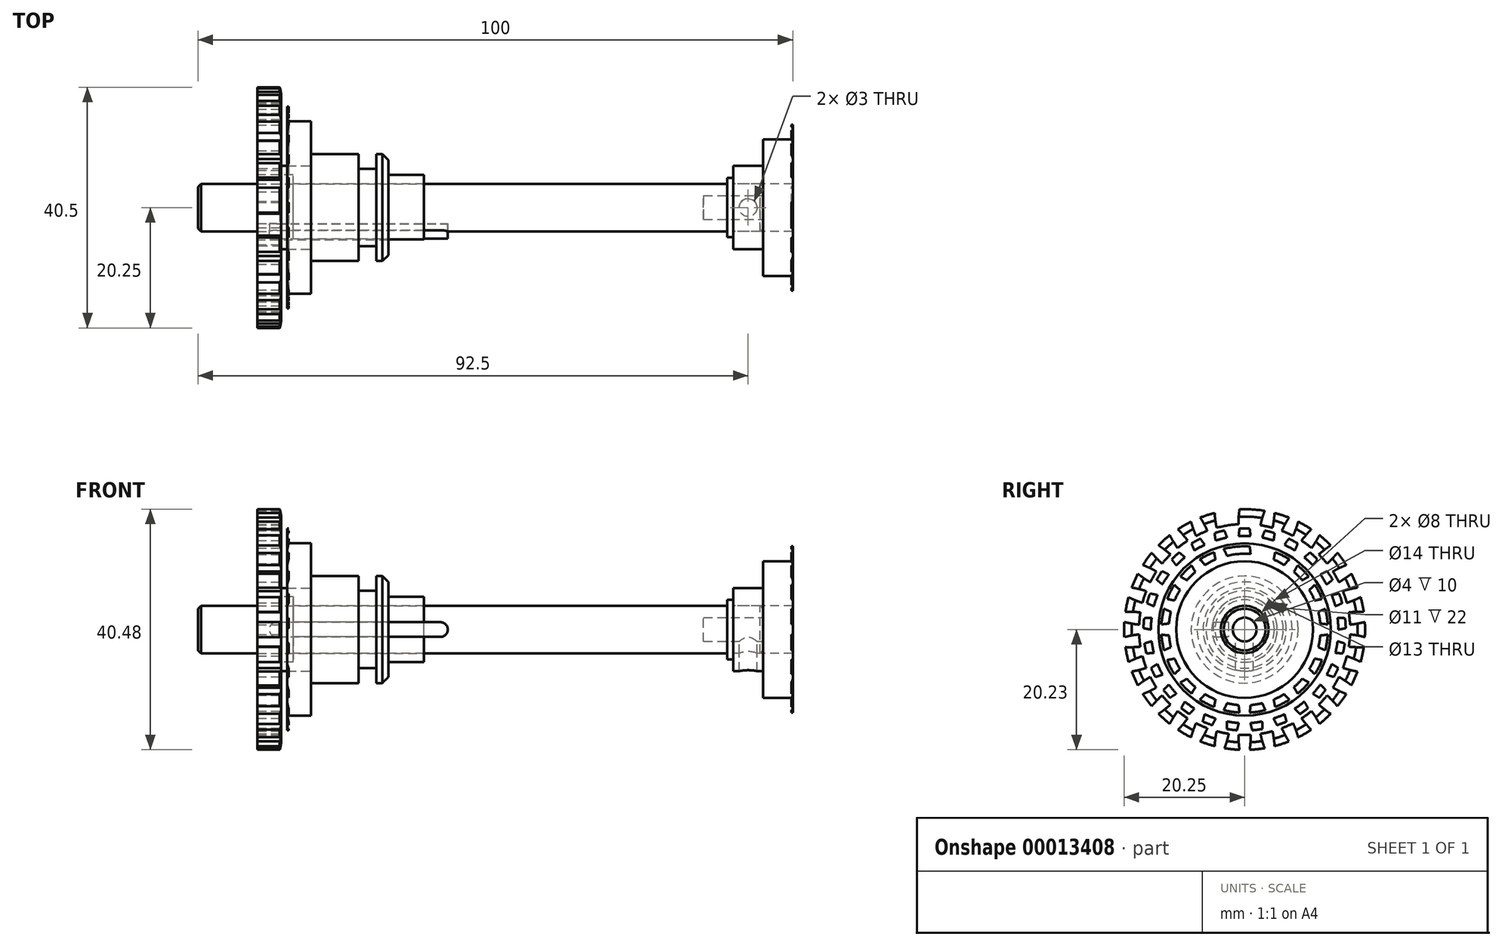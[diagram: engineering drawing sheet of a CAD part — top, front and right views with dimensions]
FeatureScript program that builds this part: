
annotation { "Feature Type Name" : "Feature", "Feature Type Description" : "" }
export const myFeature = defineFeature(function(context is Context, id is Id, definition is map)
    precondition{}
    {
        {
            var Q0;
            Q0=qCreatedBy(makeId("Right.planeOp"),FACE);
            var sketch = newSketch(context, id + "F0", { "sketchPlane" : qUnion([Q0])});
            skCircle(sketch, "E0", {"center": v(0, 0) * mm, "radius": 2 * mm});
            skCircle(sketch, "E1", {"center": v(0, 0) * mm, "radius": 4 * mm});
            skCircle(sketch, "E2", {"center": v(0, 0) * mm, "radius": 5 * mm});
            skSolve(sketch);
        }
        {
            var Q0;
            Q0=makeQuery(id+"F0.imprint","IMPRINT",FACE,{"disambiguationData":[TD([[makeQuery(id+"F0.imprint","IMPRINT",EDGE,{"derivedFrom":sQuery(id+"F0.wireOp",EDGE,"E0")}),-1.0]])]});
            var Q1;
            Q1=makeQuery(id+"F0.imprint","IMPRINT",FACE,{"disambiguationData":[TD([[makeQuery(id+"F0.imprint","IMPRINT",EDGE,{"derivedFrom":sQuery(id+"F0.wireOp",EDGE,"E0")}),1.0]])]});
            extrude(context, id + "F1", {"entities" : qUnion([Q0, Q1]), "oppositeDirection" : true, "depth" : 90 * mm});
        }
        {
            var Q0;
            Q0=makeQuery(id+"F0.imprint","IMPRINT",FACE,{"disambiguationData":[TD([[makeQuery(id+"F0.imprint","IMPRINT",EDGE,{"derivedFrom":sQuery(id+"F0.wireOp",EDGE,"E1")}),-1.0]])]});
            var Q1;
            Q1=makeQuery(id+"F0.imprint","IMPRINT",FACE,{"disambiguationData":[TD([[makeQuery(id+"F0.imprint","IMPRINT",EDGE,{"derivedFrom":sQuery(id+"F0.wireOp",EDGE,"E0")}),-1.0]])]});
            extrude(context, id + "F2", {"entities" : qUnion([Q0, Q1]), "operationType" : NewBodyOperationType.ADD, "oppositeDirection" : true, "depth" : 1 * mm});
        }
        {
            var Q0;
            Q0=makeQuery(id+"F0.imprint","IMPRINT",FACE,{"disambiguationData":[TD([[makeQuery(id+"F0.imprint","IMPRINT",EDGE,{"derivedFrom":sQuery(id+"F0.wireOp",EDGE,"E0")}),1.0]])]});
            extrude(context, id + "F3", {"entities" : qUnion([Q0]), "operationType" : NewBodyOperationType.REMOVE, "oppositeDirection" : true, "depth" : 5 * mm});
        }
        {
            var Q0;
            Q0=makeQuery(id+"F0.imprint","IMPRINT",FACE,{"disambiguationData":[TD([[makeQuery(id+"F0.imprint","IMPRINT",EDGE,{"derivedFrom":sQuery(id+"F0.wireOp",EDGE,"E0")}),-1.0]])]});
            extrude(context, id + "F4", {"entities" : qUnion([Q0]), "operationType" : NewBodyOperationType.ADD, "depth" : 5 * mm});
        }
        {
            var Q0;
            Q0=qCreatedBy(makeId("Front.planeOp"),FACE);
            cPlane(context, id + "F5", {"entities" : qUnion([Q0]), "cplaneType" : CPlaneType.OFFSET, "offset" : 4 * mm, "width" : 150 * mm, "height" : 150 * mm});
        }
        {
            var Q0;
            Q0=qCreatedBy(id+"F5.planeOp",FACE);
            var sketch = newSketch(context, id + "F6", { "sketchPlane" : qUnion([Q0])});
            skLineSegment(sketch, "E3.0", {"start": v(-90, 4) * mm, "end": v(-90, -4) * mm});
            skLineSegment(sketch, "E4", {"start": v(-90, 0) * mm, "end": v(-49.25, 0) * mm, "construction": true});
            skCircle(sketch, "E5", {"center": v(-49.25, 0) * mm, "radius": 1.25 * mm});
            skCircle(sketch, "E6", {"center": v(-76.75, 0) * mm, "radius": 1.25 * mm});
            skLineSegment(sketch, "E7", {"start": v(-76.75, 1.25) * mm, "end": v(-49.25, 1.25) * mm});
            skLineSegment(sketch, "E8", {"start": v(-76.75, -1.25) * mm, "end": v(-49.25, -1.25) * mm});
            skSolve(sketch);
        }
        {
            var Q0;
            {var subQ0=sQuery(id+"F6.wireOp",EDGE,"E6");var subQ2=makeQuery(id+"F6.imprint","INTERSECT",VERTEX,{"derivedFrom":[subQ0,sQuery(id+"F6.wireOp",EDGE,"E7")]});Q0=makeQuery(id+"F6.imprint","IMPRINT",FACE,{"disambiguationData":[TD([[makeQuery(id+"F6.imprint","IMPRINT",EDGE,{"disambiguationData":[TD([[subQ2,-1.0]])],"derivedFrom":subQ0}),1.0]])]});}
            var Q1;
            {var subQ1=sQuery(id+"F6.wireOp",EDGE,"E7");Q1=makeQuery(id+"F6.imprint","IMPRINT",FACE,{"disambiguationData":[TD([[makeQuery(id+"F6.imprint","IMPRINT",EDGE,{"derivedFrom":subQ1}),-1.0]])]});}
            var Q2;
            {var subQ0=sQuery(id+"F6.wireOp",EDGE,"E5");var subQ2=makeQuery(id+"F6.imprint","INTERSECT",VERTEX,{"derivedFrom":[subQ0,sQuery(id+"F6.wireOp",EDGE,"E7")]});Q2=makeQuery(id+"F6.imprint","IMPRINT",FACE,{"disambiguationData":[TD([[makeQuery(id+"F6.imprint","IMPRINT",EDGE,{"disambiguationData":[TD([[subQ2,-1.0]])],"derivedFrom":subQ0}),1.0]])]});}
            extrude(context, id + "F7", {"entities" : qUnion([Q0, Q1, Q2]), "operationType" : NewBodyOperationType.REMOVE, "oppositeDirection" : true, "depth" : 1.3 * mm});
        }
        {
            var Q0;
            {var subQ0=sQuery(id+"F6.wireOp",EDGE,"E6");var subQ2=makeQuery(id+"F6.imprint","INTERSECT",VERTEX,{"derivedFrom":[subQ0,sQuery(id+"F6.wireOp",EDGE,"E7")]});Q0=makeQuery(id+"F6.imprint","IMPRINT",FACE,{"disambiguationData":[TD([[makeQuery(id+"F6.imprint","IMPRINT",EDGE,{"disambiguationData":[TD([[subQ2,-1.0]])],"derivedFrom":subQ0}),1.0]])]});}
            var Q1;
            {var subQ1=sQuery(id+"F6.wireOp",EDGE,"E7");Q1=makeQuery(id+"F6.imprint","IMPRINT",FACE,{"disambiguationData":[TD([[makeQuery(id+"F6.imprint","IMPRINT",EDGE,{"derivedFrom":subQ1}),-1.0]])]});}
            var Q2;
            {var subQ0=sQuery(id+"F6.wireOp",EDGE,"E5");var subQ2=makeQuery(id+"F6.imprint","INTERSECT",VERTEX,{"derivedFrom":[subQ0,sQuery(id+"F6.wireOp",EDGE,"E7")]});Q2=makeQuery(id+"F6.imprint","IMPRINT",FACE,{"disambiguationData":[TD([[makeQuery(id+"F6.imprint","IMPRINT",EDGE,{"disambiguationData":[TD([[subQ2,-1.0]])],"derivedFrom":subQ0}),1.0]])]});}
            extrude(context, id + "F8", {"entities" : qUnion([Q0, Q1, Q2]), "endBound" : BoundingType.SYMMETRIC, "depth" : 2.5 * mm});
        }
        {
            var Q0;
            Q0=makeQuery(id+"F4.opExtrude","CAP_EDGE",EDGE,{"disambiguationData":[OSD([sQuery(id+"F0.wireOp",EDGE,"E1")])],"isStart":false});
            var Q1;
            Q1=makeQuery(id+"F1.opExtrude","CAP_EDGE",EDGE,{"disambiguationData":[OSD([sQuery(id+"F0.wireOp",EDGE,"E1")])],"isStart":false});
            chamfer(context, id + "F9", {"entities" : qUnion([Q0, Q1]), "width" : 0.5 * mm, "tangentPropagation" : true});
        }
        {
            var Q0;
            Q0=qCreatedBy(makeId("Right.planeOp"),FACE);
            cPlane(context, id + "F10", {"entities" : qUnion([Q0]), "cplaneType" : CPlaneType.OFFSET, "offset" : (48 + 15) * mm, "oppositeDirection" : true, "width" : 150 * mm, "height" : 150 * mm});
        }
        {
            var Q0;
            Q0=qCreatedBy(id+"F10.planeOp",FACE);
            var sketch = newSketch(context, id + "F11", { "sketchPlane" : qUnion([Q0])});
            skCircle(sketch, "E9.0", {"center": v(0, 0) * mm, "radius": 4 * mm});
            skLineSegment(sketch, "E9.1", {"start": v(-5.36, -1.25) * mm, "end": v(-2.75, -1.25) * mm});
            skLineSegment(sketch, "E9.2", {"start": v(-5.36, 1.25) * mm, "end": v(-2.75, 1.25) * mm});
            skCircle(sketch, "E10", {"center": v(0, 0) * mm, "radius": 5.5 * mm});
            skPoint(sketch, "E11.orphan", {"position": v(-5.25, 1.25) * mm});
            skPoint(sketch, "E12.orphan", {"position": v(-5.25, -1.25) * mm});
            skSolve(sketch);
        }
        {
            var Q0;
            {var subQ3=sQuery(id+"F11.wireOp",EDGE,"E9.1");var subQ5=sQuery(id+"F11.wireOp",EDGE,"E9.0");var subQ7=makeQuery(id+"F11.imprint","INTERSECT",VERTEX,{"derivedFrom":[subQ5,subQ3]});Q0=makeQuery(id+"F11.imprint","IMPRINT",FACE,{"disambiguationData":[TD([[makeQuery(id+"F11.imprint","IMPRINT",EDGE,{"disambiguationData":[TD([[subQ7,-1.0]])],"derivedFrom":subQ5}),-1.0]])]});}
            extrude(context, id + "F12", {"entities" : qUnion([Q0]), "endBound" : BoundingType.SYMMETRIC, "depth" : 22 * mm});
        }
        {
            var Q0;
            Q0=qCreatedBy(id+"F10.planeOp",FACE);
            var sketch = newSketch(context, id + "F13", { "sketchPlane" : qUnion([Q0])});
            skCircle(sketch, "E13.1", {"center": v(0, 0) * mm, "radius": 5.5 * mm});
            skCircle(sketch, "E14", {"center": v(0, 0) * mm, "radius": 6.5 * mm});
            skCircle(sketch, "E15", {"center": v(0, 0) * mm, "radius": 7 * mm});
            skCircle(sketch, "E16", {"center": v(0, 0) * mm, "radius": 9 * mm});
            skSolve(sketch);
        }
        {
            var Q0;
            Q0=makeQuery(id+"F13.imprint","IMPRINT",FACE,{"disambiguationData":[TD([[makeQuery(id+"F13.imprint","IMPRINT",EDGE,{"derivedFrom":sQuery(id+"F13.wireOp",EDGE,"E13.1")}),-1.0]])]});
            var Q1;
            Q1=makeQuery(id+"F13.imprint","IMPRINT",FACE,{"disambiguationData":[TD([[makeQuery(id+"F13.imprint","IMPRINT",EDGE,{"derivedFrom":sQuery(id+"F13.wireOp",EDGE,"E14")}),-1.0]])]});
            var Q2;
            Q2=makeQuery(id+"F13.imprint","IMPRINT",FACE,{"disambiguationData":[TD([[makeQuery(id+"F13.imprint","IMPRINT",EDGE,{"derivedFrom":sQuery(id+"F13.wireOp",EDGE,"E15")}),-1.0]])]});
            extrude(context, id + "F14", {"entities" : qUnion([Q0, Q1, Q2]), "depth" : 5 * mm});
        }
        {
            var Q0;
            Q0=makeQuery(id+"F13.imprint","IMPRINT",FACE,{"disambiguationData":[TD([[makeQuery(id+"F13.imprint","IMPRINT",EDGE,{"derivedFrom":sQuery(id+"F13.wireOp",EDGE,"E15")}),-1.0]])]});
            var Q1;
            Q1=makeQuery(id+"F13.imprint","IMPRINT",FACE,{"disambiguationData":[TD([[makeQuery(id+"F13.imprint","IMPRINT",EDGE,{"derivedFrom":sQuery(id+"F13.wireOp",EDGE,"E14")}),-1.0]])]});
            extrude(context, id + "F15", {"entities" : qUnion([Q0, Q1]), "operationType" : NewBodyOperationType.REMOVE, "depth" : 3 * mm});
        }
        {
            var Q0;
            Q0=makeQuery(id+"F13.imprint","IMPRINT",FACE,{"disambiguationData":[TD([[makeQuery(id+"F13.imprint","IMPRINT",EDGE,{"derivedFrom":sQuery(id+"F13.wireOp",EDGE,"E13.1")}),-1.0]])]});
            extrude(context, id + "F16", {"entities" : qUnion([Q0]), "operationType" : NewBodyOperationType.ADD, "oppositeDirection" : true, "depth" : (4 + 5 + 8) * mm});
        }
        {
            var Q0;
            Q0=makeQuery(id+"F13.imprint","IMPRINT",FACE,{"disambiguationData":[TD([[makeQuery(id+"F13.imprint","IMPRINT",EDGE,{"derivedFrom":sQuery(id+"F13.wireOp",EDGE,"E14")}),-1.0]])]});
            extrude(context, id + "F17", {"entities" : qUnion([Q0]), "operationType" : NewBodyOperationType.ADD, "oppositeDirection" : true, "depth" : (5 + 8) * mm});
        }
        {
            var Q0;
            Q0=makeQuery(id+"F13.imprint","IMPRINT",FACE,{"disambiguationData":[TD([[makeQuery(id+"F13.imprint","IMPRINT",EDGE,{"derivedFrom":sQuery(id+"F13.wireOp",EDGE,"E15")}),-1.0]])]});
            extrude(context, id + "F18", {"entities" : qUnion([Q0]), "operationType" : NewBodyOperationType.ADD, "oppositeDirection" : true, "depth" : 8 * mm});
        }
        {
            var Q0;
            Q0=makeQuery(id+"F14.opExtrude","CAP_EDGE",EDGE,{"disambiguationData":[OSD([sQuery(id+"F13.wireOp",EDGE,"E16")])],"isStart":false});
            chamfer(context, id + "F19", {"entities" : qUnion([Q0]), "width" : 1 * mm, "tangentPropagation" : true});
        }
        {
            var Q0;
            Q0=makeQuery(id+"F17.opExtrude","CAP_FACE",FACE,{"disambiguationData":[OSD([sQuery(id+"F13.wireOp",EDGE,"E14"),sQuery(id+"F13.wireOp",EDGE,"E15")])],"isStart":false});
            var sketch = newSketch(context, id + "F20", { "sketchPlane" : qUnion([Q0])});
            skCircle(sketch, "E17.0", {"center": v(0, 0) * mm, "radius": 6.5 * mm});
            skCircle(sketch, "E18", {"center": v(0, 0) * mm, "radius": 17.75 * mm});
            skCircle(sketch, "E19", {"center": v(0, 0) * mm, "radius": 20.25 * mm});
            skCircle(sketch, "E20", {"center": v(0, 0) * mm, "radius": 19 * mm, "construction": true});
            skLineSegment(sketch, "E21", {"start": v(0, 0) * mm, "end": v(0, 19) * mm, "construction": true});
            skLineSegment(sketch, "E22", {"start": v(0, 19) * mm, "end": v(0, 20.25) * mm, "construction": true});
            skLineSegment(sketch, "E23", {"start": v(0, 17.75) * mm, "end": v(15, 17.75) * mm, "construction": true});
            skLineSegment(sketch, "E24", {"start": v(0, 0) * mm, "end": v(-1, 18.97) * mm, "construction": true});
            skArc(sketch, "E25", {"start": v(-0.85, 20.23) * mm, "mid": v(-1, 18.98) * mm, "end": v(-1.04, 17.72) * mm});
            skArc(sketch, "E26.0.MirrorCS", {"start": v(0.85, 20.23) * mm, "mid": v(1, 18.98) * mm, "end": v(1.04, 17.72) * mm});
            skArc(sketch, "E27.1.0", {"start": v(-3.38, 19.97) * mm, "mid": v(-2.97, 18.77) * mm, "end": v(-2.67, 17.55) * mm});
            skArc(sketch, "E27.1.1", {"start": v(-5.04, 19.61) * mm, "mid": v(-4.92, 18.36) * mm, "end": v(-4.7, 17.12) * mm});
            skArc(sketch, "E27.2.0", {"start": v(-7.45, 18.83) * mm, "mid": v(-6.81, 17.74) * mm, "end": v(-6.26, 16.61) * mm});
            skArc(sketch, "E27.2.1", {"start": v(-9, 18.14) * mm, "mid": v(-8.63, 16.93) * mm, "end": v(-8.16, 15.76) * mm});
            skArc(sketch, "E27.3.0", {"start": v(-11.2, 16.87) * mm, "mid": v(-10.35, 15.94) * mm, "end": v(-9.57, 14.95) * mm});
            skArc(sketch, "E27.3.1", {"start": v(-12.58, 15.87) * mm, "mid": v(-11.96, 14.77) * mm, "end": v(-11.26, 13.72) * mm});
            skArc(sketch, "E27.4.0", {"start": v(-14.47, 14.17) * mm, "mid": v(-13.44, 13.44) * mm, "end": v(-12.47, 12.63) * mm});
            skArc(sketch, "E27.4.1", {"start": v(-15.6, 12.9) * mm, "mid": v(-14.77, 11.96) * mm, "end": v(-13.86, 11.08) * mm});
            skArc(sketch, "E27.5.0", {"start": v(-17.1, 10.85) * mm, "mid": v(-15.94, 10.35) * mm, "end": v(-14.82, 9.76) * mm});
            skArc(sketch, "E27.5.1", {"start": v(-17.95, 9.38) * mm, "mid": v(-16.93, 8.63) * mm, "end": v(-15.87, 7.96) * mm});
            skArc(sketch, "E27.6.0", {"start": v(-18.98, 7.06) * mm, "mid": v(-17.74, 6.81) * mm, "end": v(-16.53, 6.47) * mm});
            skArc(sketch, "E27.6.1", {"start": v(-19.5, 5.45) * mm, "mid": v(-18.36, 4.92) * mm, "end": v(-17.17, 4.49) * mm});
            skArc(sketch, "E27.7.0", {"start": v(-20.03, 2.96) * mm, "mid": v(-18.77, 2.97) * mm, "end": v(-17.51, 2.89) * mm});
            skArc(sketch, "E27.7.1", {"start": v(-20.21, 1.27) * mm, "mid": v(-18.98, 1) * mm, "end": v(-17.73, 0.82) * mm});
            skArc(sketch, "E27.8.0", {"start": v(-20.21, -1.27) * mm, "mid": v(-18.98, -1) * mm, "end": v(-17.73, -0.82) * mm});
            skArc(sketch, "E27.8.1", {"start": v(-20.03, -2.96) * mm, "mid": v(-18.77, -2.97) * mm, "end": v(-17.51, -2.89) * mm});
            skArc(sketch, "E27.9.0", {"start": v(-19.5, -5.45) * mm, "mid": v(-18.36, -4.92) * mm, "end": v(-17.17, -4.49) * mm});
            skArc(sketch, "E27.9.1", {"start": v(-18.98, -7.06) * mm, "mid": v(-17.74, -6.81) * mm, "end": v(-16.53, -6.47) * mm});
            skArc(sketch, "E27.10.0", {"start": v(-17.95, -9.38) * mm, "mid": v(-16.93, -8.63) * mm, "end": v(-15.87, -7.96) * mm});
            skArc(sketch, "E27.10.1", {"start": v(-17.1, -10.85) * mm, "mid": v(-15.94, -10.35) * mm, "end": v(-14.82, -9.76) * mm});
            skArc(sketch, "E27.11.0", {"start": v(-15.6, -12.9) * mm, "mid": v(-14.77, -11.96) * mm, "end": v(-13.86, -11.08) * mm});
            skArc(sketch, "E27.11.1", {"start": v(-14.47, -14.17) * mm, "mid": v(-13.44, -13.44) * mm, "end": v(-12.47, -12.63) * mm});
            skArc(sketch, "E27.12.0", {"start": v(-12.58, -15.87) * mm, "mid": v(-11.96, -14.77) * mm, "end": v(-11.26, -13.72) * mm});
            skArc(sketch, "E27.12.1", {"start": v(-11.2, -16.87) * mm, "mid": v(-10.35, -15.94) * mm, "end": v(-9.57, -14.95) * mm});
            skArc(sketch, "E27.13.0", {"start": v(-9, -18.14) * mm, "mid": v(-8.63, -16.93) * mm, "end": v(-8.16, -15.76) * mm});
            skArc(sketch, "E27.13.1", {"start": v(-7.45, -18.83) * mm, "mid": v(-6.81, -17.74) * mm, "end": v(-6.26, -16.61) * mm});
            skArc(sketch, "E27.14.0", {"start": v(-5.04, -19.61) * mm, "mid": v(-4.92, -18.36) * mm, "end": v(-4.7, -17.12) * mm});
            skArc(sketch, "E27.14.1", {"start": v(-3.38, -19.97) * mm, "mid": v(-2.97, -18.77) * mm, "end": v(-2.67, -17.55) * mm});
            skArc(sketch, "E27.15.0", {"start": v(-0.85, -20.23) * mm, "mid": v(-1, -18.98) * mm, "end": v(-1.04, -17.72) * mm});
            skArc(sketch, "E27.15.1", {"start": v(0.85, -20.23) * mm, "mid": v(1, -18.98) * mm, "end": v(1.04, -17.72) * mm});
            skArc(sketch, "E27.16.0", {"start": v(3.38, -19.97) * mm, "mid": v(2.97, -18.77) * mm, "end": v(2.67, -17.55) * mm});
            skArc(sketch, "E27.16.1", {"start": v(5.04, -19.61) * mm, "mid": v(4.92, -18.36) * mm, "end": v(4.7, -17.12) * mm});
            skArc(sketch, "E27.17.0", {"start": v(7.45, -18.83) * mm, "mid": v(6.81, -17.74) * mm, "end": v(6.26, -16.61) * mm});
            skArc(sketch, "E27.17.1", {"start": v(9, -18.14) * mm, "mid": v(8.63, -16.93) * mm, "end": v(8.16, -15.76) * mm});
            skArc(sketch, "E27.18.0", {"start": v(11.2, -16.87) * mm, "mid": v(10.35, -15.94) * mm, "end": v(9.57, -14.95) * mm});
            skArc(sketch, "E27.18.1", {"start": v(12.58, -15.87) * mm, "mid": v(11.96, -14.77) * mm, "end": v(11.26, -13.72) * mm});
            skArc(sketch, "E27.19.0", {"start": v(14.47, -14.17) * mm, "mid": v(13.44, -13.44) * mm, "end": v(12.47, -12.63) * mm});
            skArc(sketch, "E27.19.1", {"start": v(15.6, -12.9) * mm, "mid": v(14.77, -11.96) * mm, "end": v(13.86, -11.08) * mm});
            skArc(sketch, "E27.20.0", {"start": v(17.1, -10.85) * mm, "mid": v(15.94, -10.35) * mm, "end": v(14.82, -9.76) * mm});
            skArc(sketch, "E27.20.1", {"start": v(17.95, -9.38) * mm, "mid": v(16.93, -8.63) * mm, "end": v(15.87, -7.96) * mm});
            skArc(sketch, "E27.21.0", {"start": v(18.98, -7.06) * mm, "mid": v(17.74, -6.81) * mm, "end": v(16.53, -6.47) * mm});
            skArc(sketch, "E27.21.1", {"start": v(19.5, -5.45) * mm, "mid": v(18.36, -4.92) * mm, "end": v(17.17, -4.49) * mm});
            skArc(sketch, "E27.22.0", {"start": v(20.03, -2.96) * mm, "mid": v(18.77, -2.97) * mm, "end": v(17.51, -2.89) * mm});
            skArc(sketch, "E27.22.1", {"start": v(20.21, -1.27) * mm, "mid": v(18.98, -1) * mm, "end": v(17.73, -0.82) * mm});
            skArc(sketch, "E27.23.0", {"start": v(20.21, 1.27) * mm, "mid": v(18.98, 1) * mm, "end": v(17.73, 0.82) * mm});
            skArc(sketch, "E27.23.1", {"start": v(20.03, 2.96) * mm, "mid": v(18.77, 2.97) * mm, "end": v(17.51, 2.89) * mm});
            skArc(sketch, "E27.24.0", {"start": v(19.5, 5.45) * mm, "mid": v(18.36, 4.92) * mm, "end": v(17.17, 4.49) * mm});
            skArc(sketch, "E27.24.1", {"start": v(18.98, 7.06) * mm, "mid": v(17.74, 6.81) * mm, "end": v(16.53, 6.47) * mm});
            skArc(sketch, "E27.25.0", {"start": v(17.95, 9.38) * mm, "mid": v(16.93, 8.63) * mm, "end": v(15.87, 7.96) * mm});
            skArc(sketch, "E27.25.1", {"start": v(17.1, 10.85) * mm, "mid": v(15.94, 10.35) * mm, "end": v(14.82, 9.76) * mm});
            skArc(sketch, "E27.26.0", {"start": v(15.6, 12.9) * mm, "mid": v(14.77, 11.96) * mm, "end": v(13.86, 11.08) * mm});
            skArc(sketch, "E27.26.1", {"start": v(14.47, 14.17) * mm, "mid": v(13.44, 13.44) * mm, "end": v(12.47, 12.63) * mm});
            skArc(sketch, "E27.27.0", {"start": v(12.58, 15.87) * mm, "mid": v(11.96, 14.77) * mm, "end": v(11.26, 13.72) * mm});
            skArc(sketch, "E27.27.1", {"start": v(11.2, 16.87) * mm, "mid": v(10.35, 15.94) * mm, "end": v(9.57, 14.95) * mm});
            skArc(sketch, "E27.28.0", {"start": v(9, 18.14) * mm, "mid": v(8.63, 16.93) * mm, "end": v(8.16, 15.76) * mm});
            skArc(sketch, "E27.28.1", {"start": v(7.45, 18.83) * mm, "mid": v(6.81, 17.74) * mm, "end": v(6.26, 16.61) * mm});
            skArc(sketch, "E27.29.0", {"start": v(5.04, 19.61) * mm, "mid": v(4.92, 18.36) * mm, "end": v(4.7, 17.12) * mm});
            skArc(sketch, "E27.29.1", {"start": v(3.38, 19.97) * mm, "mid": v(2.97, 18.77) * mm, "end": v(2.67, 17.55) * mm});
            skSolve(sketch);
        }
        {
            var Q0;
            Q0=makeQuery(id+"F20.imprint","IMPRINT",FACE,{"disambiguationData":[TD([[makeQuery(id+"F20.imprint","IMPRINT",EDGE,{"derivedFrom":makeQuery(id+"F17.opExtrude","CAP_EDGE",EDGE,{"disambiguationData":[OSD([sQuery(id+"F13.wireOp",EDGE,"E15")])],"isStart":false})}),1.0]])]});
            var Q1;
            Q1=makeQuery(id+"F20.imprint","IMPRINT",FACE,{"disambiguationData":[TD([[makeQuery(id+"F20.imprint","IMPRINT",EDGE,{"derivedFrom":sQuery(id+"F20.wireOp",EDGE,"E17.0")}),1.0]])]});
            var Q2;
            {var subQ1=sQuery(id+"F20.wireOp",EDGE,"E25");Q2=makeQuery(id+"F20.imprint","IMPRINT",FACE,{"disambiguationData":[TD([[makeQuery(id+"F20.imprint","IMPRINT",EDGE,{"derivedFrom":subQ1}),1.0]])]});}
            var Q3;
            {var subQ1=sQuery(id+"F20.wireOp",EDGE,"E27.1.0");Q3=makeQuery(id+"F20.imprint","IMPRINT",FACE,{"disambiguationData":[TD([[makeQuery(id+"F20.imprint","IMPRINT",EDGE,{"derivedFrom":subQ1}),-1.0]])]});}
            var Q4;
            {var subQ1=sQuery(id+"F20.wireOp",EDGE,"E27.2.0");Q4=makeQuery(id+"F20.imprint","IMPRINT",FACE,{"disambiguationData":[TD([[makeQuery(id+"F20.imprint","IMPRINT",EDGE,{"derivedFrom":subQ1}),-1.0]])]});}
            var Q5;
            {var subQ1=sQuery(id+"F20.wireOp",EDGE,"E27.3.0");Q5=makeQuery(id+"F20.imprint","IMPRINT",FACE,{"disambiguationData":[TD([[makeQuery(id+"F20.imprint","IMPRINT",EDGE,{"derivedFrom":subQ1}),-1.0]])]});}
            var Q6;
            {var subQ1=sQuery(id+"F20.wireOp",EDGE,"E27.4.0");Q6=makeQuery(id+"F20.imprint","IMPRINT",FACE,{"disambiguationData":[TD([[makeQuery(id+"F20.imprint","IMPRINT",EDGE,{"derivedFrom":subQ1}),-1.0]])]});}
            var Q7;
            {var subQ1=sQuery(id+"F20.wireOp",EDGE,"E27.5.0");Q7=makeQuery(id+"F20.imprint","IMPRINT",FACE,{"disambiguationData":[TD([[makeQuery(id+"F20.imprint","IMPRINT",EDGE,{"derivedFrom":subQ1}),-1.0]])]});}
            var Q8;
            {var subQ1=sQuery(id+"F20.wireOp",EDGE,"E27.6.0");Q8=makeQuery(id+"F20.imprint","IMPRINT",FACE,{"disambiguationData":[TD([[makeQuery(id+"F20.imprint","IMPRINT",EDGE,{"derivedFrom":subQ1}),-1.0]])]});}
            var Q9;
            {var subQ1=sQuery(id+"F20.wireOp",EDGE,"E27.7.0");Q9=makeQuery(id+"F20.imprint","IMPRINT",FACE,{"disambiguationData":[TD([[makeQuery(id+"F20.imprint","IMPRINT",EDGE,{"derivedFrom":subQ1}),-1.0]])]});}
            var Q10;
            {var subQ1=sQuery(id+"F20.wireOp",EDGE,"E27.8.0");Q10=makeQuery(id+"F20.imprint","IMPRINT",FACE,{"disambiguationData":[TD([[makeQuery(id+"F20.imprint","IMPRINT",EDGE,{"derivedFrom":subQ1}),-1.0]])]});}
            var Q11;
            {var subQ1=sQuery(id+"F20.wireOp",EDGE,"E27.9.0");Q11=makeQuery(id+"F20.imprint","IMPRINT",FACE,{"disambiguationData":[TD([[makeQuery(id+"F20.imprint","IMPRINT",EDGE,{"derivedFrom":subQ1}),-1.0]])]});}
            var Q12;
            {var subQ1=sQuery(id+"F20.wireOp",EDGE,"E27.10.0");Q12=makeQuery(id+"F20.imprint","IMPRINT",FACE,{"disambiguationData":[TD([[makeQuery(id+"F20.imprint","IMPRINT",EDGE,{"derivedFrom":subQ1}),-1.0]])]});}
            var Q13;
            {var subQ1=sQuery(id+"F20.wireOp",EDGE,"E27.11.0");Q13=makeQuery(id+"F20.imprint","IMPRINT",FACE,{"disambiguationData":[TD([[makeQuery(id+"F20.imprint","IMPRINT",EDGE,{"derivedFrom":subQ1}),-1.0]])]});}
            var Q14;
            {var subQ1=sQuery(id+"F20.wireOp",EDGE,"E27.12.0");Q14=makeQuery(id+"F20.imprint","IMPRINT",FACE,{"disambiguationData":[TD([[makeQuery(id+"F20.imprint","IMPRINT",EDGE,{"derivedFrom":subQ1}),-1.0]])]});}
            var Q15;
            {var subQ1=sQuery(id+"F20.wireOp",EDGE,"E27.14.0");Q15=makeQuery(id+"F20.imprint","IMPRINT",FACE,{"disambiguationData":[TD([[makeQuery(id+"F20.imprint","IMPRINT",EDGE,{"derivedFrom":subQ1}),-1.0]])]});}
            var Q16;
            {var subQ2=sQuery(id+"F20.wireOp",EDGE,"E27.15.0");Q16=makeQuery(id+"F20.imprint","IMPRINT",FACE,{"disambiguationData":[TD([[makeQuery(id+"F20.imprint","IMPRINT",EDGE,{"derivedFrom":subQ2}),-1.0]])]});}
            var Q17;
            {var subQ1=sQuery(id+"F20.wireOp",EDGE,"E27.13.0");Q17=makeQuery(id+"F20.imprint","IMPRINT",FACE,{"disambiguationData":[TD([[makeQuery(id+"F20.imprint","IMPRINT",EDGE,{"derivedFrom":subQ1}),-1.0]])]});}
            var Q18;
            {var subQ2=sQuery(id+"F20.wireOp",EDGE,"E27.16.0");Q18=makeQuery(id+"F20.imprint","IMPRINT",FACE,{"disambiguationData":[TD([[makeQuery(id+"F20.imprint","IMPRINT",EDGE,{"derivedFrom":subQ2}),-1.0]])]});}
            var Q19;
            {var subQ1=sQuery(id+"F20.wireOp",EDGE,"E27.17.0");Q19=makeQuery(id+"F20.imprint","IMPRINT",FACE,{"disambiguationData":[TD([[makeQuery(id+"F20.imprint","IMPRINT",EDGE,{"derivedFrom":subQ1}),-1.0]])]});}
            var Q20;
            {var subQ1=sQuery(id+"F20.wireOp",EDGE,"E27.18.0");Q20=makeQuery(id+"F20.imprint","IMPRINT",FACE,{"disambiguationData":[TD([[makeQuery(id+"F20.imprint","IMPRINT",EDGE,{"derivedFrom":subQ1}),-1.0]])]});}
            var Q21;
            {var subQ1=sQuery(id+"F20.wireOp",EDGE,"E27.19.0");Q21=makeQuery(id+"F20.imprint","IMPRINT",FACE,{"disambiguationData":[TD([[makeQuery(id+"F20.imprint","IMPRINT",EDGE,{"derivedFrom":subQ1}),-1.0]])]});}
            var Q22;
            {var subQ1=sQuery(id+"F20.wireOp",EDGE,"E27.20.0");Q22=makeQuery(id+"F20.imprint","IMPRINT",FACE,{"disambiguationData":[TD([[makeQuery(id+"F20.imprint","IMPRINT",EDGE,{"derivedFrom":subQ1}),-1.0]])]});}
            var Q23;
            {var subQ1=sQuery(id+"F20.wireOp",EDGE,"E27.21.0");Q23=makeQuery(id+"F20.imprint","IMPRINT",FACE,{"disambiguationData":[TD([[makeQuery(id+"F20.imprint","IMPRINT",EDGE,{"derivedFrom":subQ1}),-1.0]])]});}
            var Q24;
            {var subQ1=sQuery(id+"F20.wireOp",EDGE,"E27.22.0");Q24=makeQuery(id+"F20.imprint","IMPRINT",FACE,{"disambiguationData":[TD([[makeQuery(id+"F20.imprint","IMPRINT",EDGE,{"derivedFrom":subQ1}),-1.0]])]});}
            var Q25;
            {var subQ1=sQuery(id+"F20.wireOp",EDGE,"E27.23.0");Q25=makeQuery(id+"F20.imprint","IMPRINT",FACE,{"disambiguationData":[TD([[makeQuery(id+"F20.imprint","IMPRINT",EDGE,{"derivedFrom":subQ1}),-1.0]])]});}
            var Q26;
            {var subQ1=sQuery(id+"F20.wireOp",EDGE,"E27.24.0");Q26=makeQuery(id+"F20.imprint","IMPRINT",FACE,{"disambiguationData":[TD([[makeQuery(id+"F20.imprint","IMPRINT",EDGE,{"derivedFrom":subQ1}),-1.0]])]});}
            var Q27;
            {var subQ1=sQuery(id+"F20.wireOp",EDGE,"E27.25.0");Q27=makeQuery(id+"F20.imprint","IMPRINT",FACE,{"disambiguationData":[TD([[makeQuery(id+"F20.imprint","IMPRINT",EDGE,{"derivedFrom":subQ1}),-1.0]])]});}
            var Q28;
            {var subQ1=sQuery(id+"F20.wireOp",EDGE,"E27.26.0");Q28=makeQuery(id+"F20.imprint","IMPRINT",FACE,{"disambiguationData":[TD([[makeQuery(id+"F20.imprint","IMPRINT",EDGE,{"derivedFrom":subQ1}),-1.0]])]});}
            var Q29;
            {var subQ1=sQuery(id+"F20.wireOp",EDGE,"E27.27.0");Q29=makeQuery(id+"F20.imprint","IMPRINT",FACE,{"disambiguationData":[TD([[makeQuery(id+"F20.imprint","IMPRINT",EDGE,{"derivedFrom":subQ1}),-1.0]])]});}
            var Q30;
            {var subQ1=sQuery(id+"F20.wireOp",EDGE,"E27.28.0");Q30=makeQuery(id+"F20.imprint","IMPRINT",FACE,{"disambiguationData":[TD([[makeQuery(id+"F20.imprint","IMPRINT",EDGE,{"derivedFrom":subQ1}),-1.0]])]});}
            var Q31;
            {var subQ1=sQuery(id+"F20.wireOp",EDGE,"E27.29.0");Q31=makeQuery(id+"F20.imprint","IMPRINT",FACE,{"disambiguationData":[TD([[makeQuery(id+"F20.imprint","IMPRINT",EDGE,{"derivedFrom":subQ1}),-1.0]])]});}
            extrude(context, id + "F21", {"entities" : qUnion([Q0, Q1, Q2, Q3, Q4, Q5, Q6, Q7, Q8, Q9, Q10, Q11, Q12, Q13, Q14, Q15, Q16, Q17, Q18, Q19, Q20, Q21, Q22, Q23, Q24, Q25, Q26, Q27, Q28, Q29, Q30, Q31]), "depth" : 4 * mm});
        }
        {
            var Q0;
            Q0=qCreatedBy(makeId("Front.planeOp"),FACE);
            var sketch = newSketch(context, id + "F22", { "sketchPlane" : qUnion([Q0])});
            skLineSegment(sketch, "E28.0", {"start": v(-76, -20.25) * mm, "end": v(-76, 20.25) * mm});
            skLineSegment(sketch, "E28.1", {"start": v(-76, -17.75) * mm, "end": v(-76, 17.75) * mm});
            skLineSegment(sketch, "E28.2", {"start": v(-76, -19) * mm, "end": v(-76, 19) * mm});
            skLineSegment(sketch, "E29", {"start": v(-76, 20.25) * mm, "end": v(-80, 20.25) * mm});
            skLineSegment(sketch, "E30", {"start": v(-80, 20.25) * mm, "end": v(-80, 17.75) * mm});
            skLineSegment(sketch, "E31", {"start": v(-76, 19) * mm, "end": v(-80, 19) * mm, "construction": true});
            skLineSegment(sketch, "E32", {"start": v(-78, 20.25) * mm, "end": v(-78, 19) * mm, "construction": true});
            skLineSegment(sketch, "E33", {"start": v(-76, 0) * mm, "end": v(-86.77, 0) * mm, "construction": true});
            skLineSegment(sketch, "E34", {"start": v(-76, 17.75) * mm, "end": v(-86, 17.75) * mm, "construction": true});
            skArc(sketch, "E35", {"start": v(-76, 19) * mm, "mid": v(-76.1, 19.63) * mm, "end": v(-76.24, 20.25) * mm});
            skArc(sketch, "E36.0.MirrorCS", {"start": v(-80, 19) * mm, "mid": v(-79.9, 19.63) * mm, "end": v(-79.76, 20.25) * mm});
            skSolve(sketch);
        }
        {
            var Q0;
            {var subQ0=sQuery(id+"F22.wireOp",EDGE,"E35");Q0=makeQuery(id+"F22.imprint","IMPRINT",FACE,{"disambiguationData":[TD([[makeQuery(id+"F22.imprint","IMPRINT",EDGE,{"derivedFrom":subQ0}),-1.0]])]});}
            var Q1;
            {var subQ0=sQuery(id+"F22.wireOp",EDGE,"E36.0.MirrorCS");Q1=makeQuery(id+"F22.imprint","IMPRINT",FACE,{"disambiguationData":[TD([[makeQuery(id+"F22.imprint","IMPRINT",EDGE,{"derivedFrom":subQ0}),1.0]])]});}
            var Q2;
            Q2=sQuery(id+"F22.wireOp",EDGE,"E33");
            revolve(context, id + "F23", {"operationType" : NewBodyOperationType.REMOVE, "entities" : qUnion([Q0, Q1]), "axis" : qUnion([Q2]), "revolveType" : RevolveType.FULL, "oppositeDirection" : true});
        }
        {
            var Q0;
            Q0=makeQuery(id+"F18.opExtrude","CAP_FACE",FACE,{"disambiguationData":[OSD([sQuery(id+"F13.wireOp",EDGE,"E15"),sQuery(id+"F13.wireOp",EDGE,"E16")])],"isStart":false});
            var sketch = newSketch(context, id + "F24", { "sketchPlane" : qUnion([Q0])});
            skCircle(sketch, "E37", {"center": v(0, 0) * mm, "radius": 14.5 * mm});
            skCircle(sketch, "E38", {"center": v(0, 0) * mm, "radius": 17 * mm});
            skCircle(sketch, "E39", {"center": v(0, 0) * mm, "radius": 15.75 * mm, "construction": true});
            skLineSegment(sketch, "E40", {"start": v(0, 0) * mm, "end": v(0, 17) * mm, "construction": true});
            skLineSegment(sketch, "E41", {"start": v(0, 0) * mm, "end": v(-0.99, 15.72) * mm, "construction": true});
            skLineSegment(sketch, "E42", {"start": v(0, 14.5) * mm, "end": v(15, 14.5) * mm, "construction": true});
            skArc(sketch, "E43", {"start": v(-0.84, 16.98) * mm, "mid": v(-0.99, 15.72) * mm, "end": v(-1.04, 14.46) * mm});
            skArc(sketch, "E44.0.MirrorCS", {"start": v(0.84, 16.98) * mm, "mid": v(0.99, 15.72) * mm, "end": v(1.04, 14.46) * mm});
            skArc(sketch, "E45.1.0", {"start": v(-5.04, 16.24) * mm, "mid": v(-4.87, 14.98) * mm, "end": v(-4.6, 13.75) * mm});
            skArc(sketch, "E45.1.1", {"start": v(-3.4, 16.66) * mm, "mid": v(-2.95, 15.48) * mm, "end": v(-2.6, 14.27) * mm});
            skArc(sketch, "E45.2.0", {"start": v(-8.92, 14.47) * mm, "mid": v(-8.44, 13.3) * mm, "end": v(-7.87, 12.18) * mm});
            skArc(sketch, "E45.2.1", {"start": v(-7.44, 15.28) * mm, "mid": v(-6.7, 14.26) * mm, "end": v(-6.06, 13.17) * mm});
            skArc(sketch, "E45.3.0", {"start": v(-12.24, 11.8) * mm, "mid": v(-11.48, 10.79) * mm, "end": v(-10.66, 9.83) * mm});
            skArc(sketch, "E45.3.1", {"start": v(-11, 12.95) * mm, "mid": v(-10.04, 12.14) * mm, "end": v(-9.15, 11.25) * mm});
            skArc(sketch, "E45.4.0", {"start": v(-14.79, 8.39) * mm, "mid": v(-13.8, 7.6) * mm, "end": v(-12.77, 6.88) * mm});
            skArc(sketch, "E45.4.1", {"start": v(-13.88, 9.8) * mm, "mid": v(-12.75, 9.26) * mm, "end": v(-11.66, 8.62) * mm});
            skArc(sketch, "E45.5.0", {"start": v(-16.4, 4.45) * mm, "mid": v(-15.26, 3.92) * mm, "end": v(-14.08, 3.48) * mm});
            skArc(sketch, "E45.5.1", {"start": v(-15.89, 6.05) * mm, "mid": v(-14.65, 5.8) * mm, "end": v(-13.44, 5.45) * mm});
            skArc(sketch, "E45.6.0", {"start": v(-17, 0.23) * mm, "mid": v(-15.76, 0) * mm, "end": v(-14.5, -0.13) * mm});
            skArc(sketch, "E45.6.1", {"start": v(-16.9, 1.9) * mm, "mid": v(-15.63, 1.97) * mm, "end": v(-14.37, 1.94) * mm});
            skArc(sketch, "E45.7.0", {"start": v(-16.52, -4) * mm, "mid": v(-15.26, -3.92) * mm, "end": v(-14.01, -3.73) * mm});
            skArc(sketch, "E45.7.1", {"start": v(-16.84, -2.35) * mm, "mid": v(-15.63, -1.98) * mm, "end": v(-14.4, -1.7) * mm});
            skArc(sketch, "E45.8.0", {"start": v(-15, -8) * mm, "mid": v(-13.8, -7.59) * mm, "end": v(-12.65, -7.1) * mm});
            skArc(sketch, "E45.8.1", {"start": v(-15.72, -6.47) * mm, "mid": v(-14.65, -5.8) * mm, "end": v(-13.53, -5.22) * mm});
            skArc(sketch, "E45.9.0", {"start": v(-12.55, -11.47) * mm, "mid": v(-11.49, -10.79) * mm, "end": v(-10.48, -10.02) * mm});
            skArc(sketch, "E45.9.1", {"start": v(-13.62, -10.17) * mm, "mid": v(-12.75, -9.26) * mm, "end": v(-11.8, -8.42) * mm});
            skArc(sketch, "E45.10.0", {"start": v(-9.3, -14.23) * mm, "mid": v(-8.44, -13.3) * mm, "end": v(-7.66, -12.3) * mm});
            skArc(sketch, "E45.10.1", {"start": v(-10.66, -13.24) * mm, "mid": v(-10.04, -12.14) * mm, "end": v(-9.34, -11.1) * mm});
            skArc(sketch, "E45.11.0", {"start": v(-5.47, -16.1) * mm, "mid": v(-4.87, -14.98) * mm, "end": v(-4.36, -13.83) * mm});
            skArc(sketch, "E45.11.1", {"start": v(-7.03, -15.48) * mm, "mid": v(-6.7, -14.26) * mm, "end": v(-6.29, -13.07) * mm});
            skArc(sketch, "E45.12.0", {"start": v(-1.3, -16.95) * mm, "mid": v(-1, -15.72) * mm, "end": v(-0.79, -14.48) * mm});
            skArc(sketch, "E45.12.1", {"start": v(-2.96, -16.74) * mm, "mid": v(-2.95, -15.48) * mm, "end": v(-2.84, -14.22) * mm});
            skArc(sketch, "E45.13.0", {"start": v(2.96, -16.74) * mm, "mid": v(2.95, -15.48) * mm, "end": v(2.84, -14.22) * mm});
            skArc(sketch, "E45.13.1", {"start": v(1.3, -16.95) * mm, "mid": v(1, -15.72) * mm, "end": v(0.79, -14.48) * mm});
            skArc(sketch, "E45.14.0", {"start": v(7.03, -15.48) * mm, "mid": v(6.7, -14.26) * mm, "end": v(6.29, -13.07) * mm});
            skArc(sketch, "E45.14.1", {"start": v(5.47, -16.1) * mm, "mid": v(4.87, -14.98) * mm, "end": v(4.36, -13.83) * mm});
            skArc(sketch, "E45.15.0", {"start": v(10.66, -13.24) * mm, "mid": v(10.04, -12.14) * mm, "end": v(9.34, -11.1) * mm});
            skArc(sketch, "E45.15.1", {"start": v(9.3, -14.23) * mm, "mid": v(8.44, -13.3) * mm, "end": v(7.66, -12.3) * mm});
            skArc(sketch, "E45.16.0", {"start": v(13.62, -10.17) * mm, "mid": v(12.75, -9.26) * mm, "end": v(11.8, -8.42) * mm});
            skArc(sketch, "E45.16.1", {"start": v(12.55, -11.47) * mm, "mid": v(11.49, -10.79) * mm, "end": v(10.48, -10.02) * mm});
            skArc(sketch, "E45.17.0", {"start": v(15.72, -6.47) * mm, "mid": v(14.65, -5.8) * mm, "end": v(13.53, -5.22) * mm});
            skArc(sketch, "E45.17.1", {"start": v(15, -8) * mm, "mid": v(13.8, -7.59) * mm, "end": v(12.65, -7.1) * mm});
            skArc(sketch, "E45.18.0", {"start": v(16.84, -2.35) * mm, "mid": v(15.63, -1.98) * mm, "end": v(14.4, -1.7) * mm});
            skArc(sketch, "E45.18.1", {"start": v(16.52, -4) * mm, "mid": v(15.26, -3.92) * mm, "end": v(14.01, -3.73) * mm});
            skArc(sketch, "E45.19.0", {"start": v(16.9, 1.9) * mm, "mid": v(15.63, 1.97) * mm, "end": v(14.37, 1.94) * mm});
            skArc(sketch, "E45.19.1", {"start": v(17, 0.23) * mm, "mid": v(15.76, 0) * mm, "end": v(14.5, -0.13) * mm});
            skArc(sketch, "E45.20.0", {"start": v(15.89, 6.05) * mm, "mid": v(14.65, 5.8) * mm, "end": v(13.44, 5.45) * mm});
            skArc(sketch, "E45.20.1", {"start": v(16.4, 4.45) * mm, "mid": v(15.26, 3.92) * mm, "end": v(14.08, 3.48) * mm});
            skArc(sketch, "E45.21.0", {"start": v(13.88, 9.8) * mm, "mid": v(12.75, 9.26) * mm, "end": v(11.66, 8.62) * mm});
            skArc(sketch, "E45.21.1", {"start": v(14.79, 8.39) * mm, "mid": v(13.8, 7.6) * mm, "end": v(12.77, 6.88) * mm});
            skArc(sketch, "E45.22.0", {"start": v(11, 12.95) * mm, "mid": v(10.04, 12.14) * mm, "end": v(9.15, 11.25) * mm});
            skArc(sketch, "E45.22.1", {"start": v(12.24, 11.8) * mm, "mid": v(11.48, 10.79) * mm, "end": v(10.66, 9.83) * mm});
            skArc(sketch, "E45.23.0", {"start": v(7.44, 15.28) * mm, "mid": v(6.7, 14.26) * mm, "end": v(6.06, 13.17) * mm});
            skArc(sketch, "E45.23.1", {"start": v(8.92, 14.47) * mm, "mid": v(8.44, 13.3) * mm, "end": v(7.87, 12.18) * mm});
            skArc(sketch, "E45.24.0", {"start": v(3.4, 16.66) * mm, "mid": v(2.95, 15.48) * mm, "end": v(2.6, 14.27) * mm});
            skArc(sketch, "E45.24.1", {"start": v(5.04, 16.24) * mm, "mid": v(4.87, 14.98) * mm, "end": v(4.6, 13.75) * mm});
            skSolve(sketch);
        }
        {
            var Q0;
            Q0=makeQuery(id+"F24.imprint","IMPRINT",FACE,{"disambiguationData":[TD([[makeQuery(id+"F24.imprint","IMPRINT",EDGE,{"derivedFrom":makeQuery(id+"F18.opExtrude","CAP_EDGE",EDGE,{"disambiguationData":[OSD([sQuery(id+"F13.wireOp",EDGE,"E16")])],"isStart":false})}),1.0]])]});
            var Q1;
            {var subQ1=sQuery(id+"F24.wireOp",EDGE,"E45.1.0");Q1=makeQuery(id+"F24.imprint","IMPRINT",FACE,{"disambiguationData":[TD([[makeQuery(id+"F24.imprint","IMPRINT",EDGE,{"derivedFrom":subQ1}),1.0]])]});}
            var Q2;
            {var subQ1=sQuery(id+"F24.wireOp",EDGE,"E43");Q2=makeQuery(id+"F24.imprint","IMPRINT",FACE,{"disambiguationData":[TD([[makeQuery(id+"F24.imprint","IMPRINT",EDGE,{"derivedFrom":subQ1}),1.0]])]});}
            var Q3;
            {var subQ1=sQuery(id+"F24.wireOp",EDGE,"E45.24.0");Q3=makeQuery(id+"F24.imprint","IMPRINT",FACE,{"disambiguationData":[TD([[makeQuery(id+"F24.imprint","IMPRINT",EDGE,{"derivedFrom":subQ1}),1.0]])]});}
            var Q4;
            {var subQ1=sQuery(id+"F24.wireOp",EDGE,"E45.23.0");Q4=makeQuery(id+"F24.imprint","IMPRINT",FACE,{"disambiguationData":[TD([[makeQuery(id+"F24.imprint","IMPRINT",EDGE,{"derivedFrom":subQ1}),1.0]])]});}
            var Q5;
            {var subQ1=sQuery(id+"F24.wireOp",EDGE,"E45.22.0");Q5=makeQuery(id+"F24.imprint","IMPRINT",FACE,{"disambiguationData":[TD([[makeQuery(id+"F24.imprint","IMPRINT",EDGE,{"derivedFrom":subQ1}),1.0]])]});}
            var Q6;
            {var subQ1=sQuery(id+"F24.wireOp",EDGE,"E45.21.0");Q6=makeQuery(id+"F24.imprint","IMPRINT",FACE,{"disambiguationData":[TD([[makeQuery(id+"F24.imprint","IMPRINT",EDGE,{"derivedFrom":subQ1}),1.0]])]});}
            var Q7;
            {var subQ1=sQuery(id+"F24.wireOp",EDGE,"E45.20.0");Q7=makeQuery(id+"F24.imprint","IMPRINT",FACE,{"disambiguationData":[TD([[makeQuery(id+"F24.imprint","IMPRINT",EDGE,{"derivedFrom":subQ1}),1.0]])]});}
            var Q8;
            {var subQ1=sQuery(id+"F24.wireOp",EDGE,"E45.19.0");Q8=makeQuery(id+"F24.imprint","IMPRINT",FACE,{"disambiguationData":[TD([[makeQuery(id+"F24.imprint","IMPRINT",EDGE,{"derivedFrom":subQ1}),1.0]])]});}
            var Q9;
            {var subQ1=sQuery(id+"F24.wireOp",EDGE,"E45.18.0");Q9=makeQuery(id+"F24.imprint","IMPRINT",FACE,{"disambiguationData":[TD([[makeQuery(id+"F24.imprint","IMPRINT",EDGE,{"derivedFrom":subQ1}),1.0]])]});}
            var Q10;
            {var subQ1=sQuery(id+"F24.wireOp",EDGE,"E45.17.0");Q10=makeQuery(id+"F24.imprint","IMPRINT",FACE,{"disambiguationData":[TD([[makeQuery(id+"F24.imprint","IMPRINT",EDGE,{"derivedFrom":subQ1}),1.0]])]});}
            var Q11;
            {var subQ1=sQuery(id+"F24.wireOp",EDGE,"E45.16.0");Q11=makeQuery(id+"F24.imprint","IMPRINT",FACE,{"disambiguationData":[TD([[makeQuery(id+"F24.imprint","IMPRINT",EDGE,{"derivedFrom":subQ1}),1.0]])]});}
            var Q12;
            {var subQ1=sQuery(id+"F24.wireOp",EDGE,"E45.15.0");Q12=makeQuery(id+"F24.imprint","IMPRINT",FACE,{"disambiguationData":[TD([[makeQuery(id+"F24.imprint","IMPRINT",EDGE,{"derivedFrom":subQ1}),1.0]])]});}
            var Q13;
            {var subQ1=sQuery(id+"F24.wireOp",EDGE,"E45.14.0");Q13=makeQuery(id+"F24.imprint","IMPRINT",FACE,{"disambiguationData":[TD([[makeQuery(id+"F24.imprint","IMPRINT",EDGE,{"derivedFrom":subQ1}),1.0]])]});}
            var Q14;
            {var subQ1=sQuery(id+"F24.wireOp",EDGE,"E45.13.0");Q14=makeQuery(id+"F24.imprint","IMPRINT",FACE,{"disambiguationData":[TD([[makeQuery(id+"F24.imprint","IMPRINT",EDGE,{"derivedFrom":subQ1}),1.0]])]});}
            var Q15;
            {var subQ1=sQuery(id+"F24.wireOp",EDGE,"E45.12.0");Q15=makeQuery(id+"F24.imprint","IMPRINT",FACE,{"disambiguationData":[TD([[makeQuery(id+"F24.imprint","IMPRINT",EDGE,{"derivedFrom":subQ1}),1.0]])]});}
            var Q16;
            {var subQ1=sQuery(id+"F24.wireOp",EDGE,"E45.11.0");Q16=makeQuery(id+"F24.imprint","IMPRINT",FACE,{"disambiguationData":[TD([[makeQuery(id+"F24.imprint","IMPRINT",EDGE,{"derivedFrom":subQ1}),1.0]])]});}
            var Q17;
            {var subQ1=sQuery(id+"F24.wireOp",EDGE,"E45.10.0");Q17=makeQuery(id+"F24.imprint","IMPRINT",FACE,{"disambiguationData":[TD([[makeQuery(id+"F24.imprint","IMPRINT",EDGE,{"derivedFrom":subQ1}),1.0]])]});}
            var Q18;
            {var subQ1=sQuery(id+"F24.wireOp",EDGE,"E45.9.0");Q18=makeQuery(id+"F24.imprint","IMPRINT",FACE,{"disambiguationData":[TD([[makeQuery(id+"F24.imprint","IMPRINT",EDGE,{"derivedFrom":subQ1}),1.0]])]});}
            var Q19;
            {var subQ1=sQuery(id+"F24.wireOp",EDGE,"E45.8.0");Q19=makeQuery(id+"F24.imprint","IMPRINT",FACE,{"disambiguationData":[TD([[makeQuery(id+"F24.imprint","IMPRINT",EDGE,{"derivedFrom":subQ1}),1.0]])]});}
            var Q20;
            {var subQ1=sQuery(id+"F24.wireOp",EDGE,"E45.7.0");Q20=makeQuery(id+"F24.imprint","IMPRINT",FACE,{"disambiguationData":[TD([[makeQuery(id+"F24.imprint","IMPRINT",EDGE,{"derivedFrom":subQ1}),1.0]])]});}
            var Q21;
            {var subQ1=sQuery(id+"F24.wireOp",EDGE,"E45.6.0");Q21=makeQuery(id+"F24.imprint","IMPRINT",FACE,{"disambiguationData":[TD([[makeQuery(id+"F24.imprint","IMPRINT",EDGE,{"derivedFrom":subQ1}),1.0]])]});}
            var Q22;
            {var subQ1=sQuery(id+"F24.wireOp",EDGE,"E45.5.0");Q22=makeQuery(id+"F24.imprint","IMPRINT",FACE,{"disambiguationData":[TD([[makeQuery(id+"F24.imprint","IMPRINT",EDGE,{"derivedFrom":subQ1}),1.0]])]});}
            var Q23;
            {var subQ1=sQuery(id+"F24.wireOp",EDGE,"E45.4.0");Q23=makeQuery(id+"F24.imprint","IMPRINT",FACE,{"disambiguationData":[TD([[makeQuery(id+"F24.imprint","IMPRINT",EDGE,{"derivedFrom":subQ1}),1.0]])]});}
            var Q24;
            {var subQ1=sQuery(id+"F24.wireOp",EDGE,"E45.3.0");Q24=makeQuery(id+"F24.imprint","IMPRINT",FACE,{"disambiguationData":[TD([[makeQuery(id+"F24.imprint","IMPRINT",EDGE,{"derivedFrom":subQ1}),1.0]])]});}
            var Q25;
            {var subQ1=sQuery(id+"F24.wireOp",EDGE,"E45.2.0");Q25=makeQuery(id+"F24.imprint","IMPRINT",FACE,{"disambiguationData":[TD([[makeQuery(id+"F24.imprint","IMPRINT",EDGE,{"derivedFrom":subQ1}),1.0]])]});}
            var Q26;
            Q26=makeQuery(id+"F24.imprint","IMPRINT",FACE,{"disambiguationData":[TD([[makeQuery(id+"F24.imprint","IMPRINT",EDGE,{"derivedFrom":makeQuery(id+"F18.opExtrude","CAP_EDGE",EDGE,{"disambiguationData":[OSD([sQuery(id+"F13.wireOp",EDGE,"E16")])],"isStart":false})}),-1.0]])]});
            extrude(context, id + "F25", {"entities" : qUnion([Q0, Q1, Q2, Q3, Q4, Q5, Q6, Q7, Q8, Q9, Q10, Q11, Q12, Q13, Q14, Q15, Q16, Q17, Q18, Q19, Q20, Q21, Q22, Q23, Q24, Q25, Q26]), "depth" : 4 * mm});
        }
        {
            var Q0;
            Q0=qCreatedBy(makeId("Front.planeOp"),FACE);
            var sketch = newSketch(context, id + "F26", { "sketchPlane" : qUnion([Q0])});
            skLineSegment(sketch, "E46.0", {"start": v(-71, -17) * mm, "end": v(-71, 17) * mm});
            skLineSegment(sketch, "E46.1", {"start": v(-71, -14.5) * mm, "end": v(-71, 14.5) * mm});
            skLineSegment(sketch, "E46.2", {"start": v(-71, -15.75) * mm, "end": v(-71, 15.75) * mm});
            skLineSegment(sketch, "E47.bottom", {"start": v(-71, 14.5) * mm, "end": v(-75, 14.5) * mm});
            skLineSegment(sketch, "E47.top", {"start": v(-71, 17) * mm, "end": v(-75, 17) * mm});
            skLineSegment(sketch, "E47.left", {"start": v(-71, 14.5) * mm, "end": v(-71, 17) * mm});
            skLineSegment(sketch, "E47.right", {"start": v(-75, 14.5) * mm, "end": v(-75, 17) * mm});
            skLineSegment(sketch, "E48", {"start": v(-71, 15.75) * mm, "end": v(-75, 15.75) * mm, "construction": true});
            skLineSegment(sketch, "E49", {"start": v(-73, 17) * mm, "end": v(-73, 15.75) * mm, "construction": true});
            skLineSegment(sketch, "E50", {"start": v(-71, 14.5) * mm, "end": v(-81, 14.5) * mm, "construction": true});
            skArc(sketch, "E51", {"start": v(-71, 15.75) * mm, "mid": v(-71.1, 16.38) * mm, "end": v(-71.24, 17) * mm});
            skArc(sketch, "E52.0.MirrorCS", {"start": v(-75, 15.75) * mm, "mid": v(-74.9, 16.38) * mm, "end": v(-74.76, 17) * mm});
            skLineSegment(sketch, "E53", {"start": v(-71, 0) * mm, "end": v(-77.28, 0) * mm, "construction": true});
            skSolve(sketch);
        }
        {
            var Q0;
            {var subQ0=sQuery(id+"F26.wireOp",EDGE,"E51");Q0=makeQuery(id+"F26.imprint","IMPRINT",FACE,{"disambiguationData":[TD([[makeQuery(id+"F26.imprint","IMPRINT",EDGE,{"derivedFrom":subQ0}),-1.0]])]});}
            var Q1;
            {var subQ0=sQuery(id+"F26.wireOp",EDGE,"E52.0.MirrorCS");Q1=makeQuery(id+"F26.imprint","IMPRINT",FACE,{"disambiguationData":[TD([[makeQuery(id+"F26.imprint","IMPRINT",EDGE,{"derivedFrom":subQ0}),1.0]])]});}
            var Q2;
            Q2=sQuery(id+"F26.wireOp",EDGE,"E53");
            revolve(context, id + "F27", {"operationType" : NewBodyOperationType.REMOVE, "entities" : qUnion([Q0, Q1]), "axis" : qUnion([Q2]), "revolveType" : RevolveType.FULL, "oppositeDirection" : true});
        }
        {
            var Q0;
            Q0=makeQuery(id+"F2.boolean.opBoolean","MERGE",FACE,{"derivedFrom":[makeQuery(id+"F1.opExtrude","CAP_FACE",FACE,{"disambiguationData":[OSD([sQuery(id+"F0.wireOp",EDGE,"E1")])],"isStart":true}),makeQuery(id+"F2.opExtrude","CAP_FACE",FACE,{"disambiguationData":[OSD([sQuery(id+"F0.wireOp",EDGE,"E0"),sQuery(id+"F0.wireOp",EDGE,"E2")])],"isStart":true})]});
            var sketch = newSketch(context, id + "F28", { "sketchPlane" : qUnion([Q0])});
            skCircle(sketch, "E54", {"center": v(0, 0) * mm, "radius": 7 * mm});
            skSolve(sketch);
        }
        {
            var Q0;
            Q0=makeQuery(id+"F28.imprint","IMPRINT",FACE,{"disambiguationData":[TD([[makeQuery(id+"F28.imprint","IMPRINT",EDGE,{"derivedFrom":sQuery(id+"F28.wireOp",EDGE,"E54")}),1.0]])]});
            var Q1;
            Q1=makeQuery(id+"F28.imprint","IMPRINT",FACE,{"disambiguationData":[TD([[makeQuery(id+"F28.imprint","IMPRINT",EDGE,{"derivedFrom":makeQuery(id+"F2.opExtrude","CAP_EDGE",EDGE,{"disambiguationData":[OSD([sQuery(id+"F0.wireOp",EDGE,"E2")])],"isStart":true})}),1.0]])]});
            extrude(context, id + "F29", {"entities" : qUnion([Q0, Q1]), "depth" : 5 * mm});
        }
        {
            var Q0;
            Q0=qCreatedBy(makeId("Top.planeOp"),FACE);
            var sketch = newSketch(context, id + "F30", { "sketchPlane" : qUnion([Q0])});
            skLineSegment(sketch, "E55.0", {"start": v(0, 7) * mm, "end": v(0, -7) * mm});
            skLineSegment(sketch, "E55.1", {"start": v(5, 7) * mm, "end": v(5, -7) * mm});
            skLineSegment(sketch, "E56", {"start": v(0, 0) * mm, "end": v(5, 0) * mm, "construction": true});
            skCircle(sketch, "E57", {"center": v(2.5, 0) * mm, "radius": 1.5 * mm});
            skSolve(sketch);
        }
        {
            var Q0;
            Q0=makeQuery(id+"F30.imprint","IMPRINT",FACE,{"disambiguationData":[TD([[makeQuery(id+"F30.imprint","IMPRINT",EDGE,{"derivedFrom":sQuery(id+"F30.wireOp",EDGE,"E57")}),1.0]])]});
            extrude(context, id + "F31", {"entities" : qUnion([Q0]), "operationType" : NewBodyOperationType.REMOVE, "oppositeDirection" : true, "depth" : 7 * mm});
        }
        {
            var Q0;
            Q0=makeQuery(id+"F29.opExtrude","CAP_FACE",FACE,{"disambiguationData":[OSD([sQuery(id+"F0.wireOp",EDGE,"E1"),sQuery(id+"F28.wireOp",EDGE,"E54")])],"isStart":false});
            var sketch = newSketch(context, id + "F32", { "sketchPlane" : qUnion([Q0])});
            skCircle(sketch, "E58", {"center": v(0, 0) * mm, "radius": 11.5 * mm});
            skCircle(sketch, "E59", {"center": v(0, 0) * mm, "radius": 14 * mm});
            skCircle(sketch, "E60", {"center": v(0, 0) * mm, "radius": 12.75 * mm, "construction": true});
            skLineSegment(sketch, "E61", {"start": v(0, 0) * mm, "end": v(0, 14) * mm, "construction": true});
            skLineSegment(sketch, "E62", {"start": v(0, 0) * mm, "end": v(-1, 12.71) * mm, "construction": true});
            skLineSegment(sketch, "E63", {"start": v(0, 11.5) * mm, "end": v(15, 11.5) * mm, "construction": true});
            skArc(sketch, "E64", {"start": v(-0.85, 13.97) * mm, "mid": v(-1, 12.72) * mm, "end": v(-1.05, 11.45) * mm});
            skArc(sketch, "E65.0.MirrorCS", {"start": v(0.85, 13.97) * mm, "mid": v(1, 12.72) * mm, "end": v(1.05, 11.45) * mm});
            skArc(sketch, "E66.1.0", {"start": v(-3.5, 13.55) * mm, "mid": v(-2.98, 12.4) * mm, "end": v(-2.54, 11.22) * mm});
            skArc(sketch, "E66.1.1", {"start": v(-5.13, 13.03) * mm, "mid": v(-4.88, 11.79) * mm, "end": v(-4.53, 10.57) * mm});
            skArc(sketch, "E66.2.0", {"start": v(-7.52, 11.8) * mm, "mid": v(-6.67, 10.88) * mm, "end": v(-5.89, 9.88) * mm});
            skArc(sketch, "E66.2.1", {"start": v(-8.9, 10.8) * mm, "mid": v(-8.28, 9.7) * mm, "end": v(-7.58, 8.65) * mm});
            skArc(sketch, "E66.3.0", {"start": v(-10.8, 8.9) * mm, "mid": v(-9.7, 8.28) * mm, "end": v(-8.65, 7.58) * mm});
            skArc(sketch, "E66.3.1", {"start": v(-11.8, 7.52) * mm, "mid": v(-10.88, 6.67) * mm, "end": v(-9.88, 5.89) * mm});
            skArc(sketch, "E66.4.0", {"start": v(-13.03, 5.13) * mm, "mid": v(-11.79, 4.88) * mm, "end": v(-10.57, 4.53) * mm});
            skArc(sketch, "E66.4.1", {"start": v(-13.55, 3.5) * mm, "mid": v(-12.4, 2.98) * mm, "end": v(-11.22, 2.54) * mm});
            skArc(sketch, "E66.5.0", {"start": v(-13.97, 0.85) * mm, "mid": v(-12.72, 1) * mm, "end": v(-11.45, 1.05) * mm});
            skArc(sketch, "E66.5.1", {"start": v(-13.97, -0.85) * mm, "mid": v(-12.72, -1) * mm, "end": v(-11.45, -1.05) * mm});
            skArc(sketch, "E66.6.0", {"start": v(-13.55, -3.5) * mm, "mid": v(-12.4, -2.98) * mm, "end": v(-11.22, -2.54) * mm});
            skArc(sketch, "E66.6.1", {"start": v(-13.03, -5.13) * mm, "mid": v(-11.79, -4.88) * mm, "end": v(-10.57, -4.53) * mm});
            skArc(sketch, "E66.7.0", {"start": v(-11.8, -7.52) * mm, "mid": v(-10.88, -6.67) * mm, "end": v(-9.88, -5.89) * mm});
            skArc(sketch, "E66.7.1", {"start": v(-10.8, -8.9) * mm, "mid": v(-9.7, -8.28) * mm, "end": v(-8.65, -7.58) * mm});
            skArc(sketch, "E66.8.0", {"start": v(-8.9, -10.8) * mm, "mid": v(-8.28, -9.7) * mm, "end": v(-7.58, -8.65) * mm});
            skArc(sketch, "E66.8.1", {"start": v(-7.52, -11.8) * mm, "mid": v(-6.67, -10.88) * mm, "end": v(-5.89, -9.88) * mm});
            skArc(sketch, "E66.9.0", {"start": v(-5.13, -13.03) * mm, "mid": v(-4.88, -11.79) * mm, "end": v(-4.53, -10.57) * mm});
            skArc(sketch, "E66.9.1", {"start": v(-3.5, -13.55) * mm, "mid": v(-2.98, -12.4) * mm, "end": v(-2.54, -11.22) * mm});
            skArc(sketch, "E66.10.0", {"start": v(-0.85, -13.97) * mm, "mid": v(-1, -12.72) * mm, "end": v(-1.05, -11.45) * mm});
            skArc(sketch, "E66.10.1", {"start": v(0.85, -13.97) * mm, "mid": v(1, -12.72) * mm, "end": v(1.05, -11.45) * mm});
            skArc(sketch, "E66.11.0", {"start": v(3.5, -13.55) * mm, "mid": v(2.98, -12.4) * mm, "end": v(2.54, -11.22) * mm});
            skArc(sketch, "E66.11.1", {"start": v(5.13, -13.03) * mm, "mid": v(4.88, -11.79) * mm, "end": v(4.53, -10.57) * mm});
            skArc(sketch, "E66.12.0", {"start": v(7.52, -11.8) * mm, "mid": v(6.67, -10.88) * mm, "end": v(5.89, -9.88) * mm});
            skArc(sketch, "E66.12.1", {"start": v(8.9, -10.8) * mm, "mid": v(8.28, -9.7) * mm, "end": v(7.58, -8.65) * mm});
            skArc(sketch, "E66.13.0", {"start": v(10.8, -8.9) * mm, "mid": v(9.7, -8.28) * mm, "end": v(8.65, -7.58) * mm});
            skArc(sketch, "E66.13.1", {"start": v(11.8, -7.52) * mm, "mid": v(10.88, -6.67) * mm, "end": v(9.88, -5.89) * mm});
            skArc(sketch, "E66.14.0", {"start": v(13.03, -5.13) * mm, "mid": v(11.79, -4.88) * mm, "end": v(10.57, -4.53) * mm});
            skArc(sketch, "E66.14.1", {"start": v(13.55, -3.5) * mm, "mid": v(12.4, -2.98) * mm, "end": v(11.22, -2.54) * mm});
            skArc(sketch, "E66.15.0", {"start": v(13.97, -0.85) * mm, "mid": v(12.72, -1) * mm, "end": v(11.45, -1.05) * mm});
            skArc(sketch, "E66.15.1", {"start": v(13.97, 0.85) * mm, "mid": v(12.72, 1) * mm, "end": v(11.45, 1.05) * mm});
            skArc(sketch, "E66.16.0", {"start": v(13.55, 3.5) * mm, "mid": v(12.4, 2.98) * mm, "end": v(11.22, 2.54) * mm});
            skArc(sketch, "E66.16.1", {"start": v(13.03, 5.13) * mm, "mid": v(11.79, 4.88) * mm, "end": v(10.57, 4.53) * mm});
            skArc(sketch, "E66.17.0", {"start": v(11.8, 7.52) * mm, "mid": v(10.88, 6.67) * mm, "end": v(9.88, 5.89) * mm});
            skArc(sketch, "E66.17.1", {"start": v(10.8, 8.9) * mm, "mid": v(9.7, 8.28) * mm, "end": v(8.65, 7.58) * mm});
            skArc(sketch, "E66.18.0", {"start": v(8.9, 10.8) * mm, "mid": v(8.28, 9.7) * mm, "end": v(7.58, 8.65) * mm});
            skArc(sketch, "E66.18.1", {"start": v(7.52, 11.8) * mm, "mid": v(6.67, 10.88) * mm, "end": v(5.89, 9.88) * mm});
            skArc(sketch, "E66.19.0", {"start": v(5.13, 13.03) * mm, "mid": v(4.88, 11.79) * mm, "end": v(4.53, 10.57) * mm});
            skArc(sketch, "E66.19.1", {"start": v(3.5, 13.55) * mm, "mid": v(2.98, 12.4) * mm, "end": v(2.54, 11.22) * mm});
            skSolve(sketch);
        }
        {
            var Q0;
            Q0=makeQuery(id+"F32.imprint","IMPRINT",FACE,{"disambiguationData":[TD([[makeQuery(id+"F32.imprint","IMPRINT",EDGE,{"derivedFrom":makeQuery(id+"F29.opExtrude","CAP_EDGE",EDGE,{"disambiguationData":[OSD([sQuery(id+"F28.wireOp",EDGE,"E54")])],"isStart":false})}),-1.0]])]});
            var Q1;
            Q1=makeQuery(id+"F32.imprint","IMPRINT",FACE,{"disambiguationData":[TD([[makeQuery(id+"F32.imprint","IMPRINT",EDGE,{"derivedFrom":makeQuery(id+"F29.opExtrude","CAP_EDGE",EDGE,{"disambiguationData":[OSD([sQuery(id+"F28.wireOp",EDGE,"E54")])],"isStart":false})}),1.0]])]});
            var Q2;
            {var subQ0=sQuery(id+"F32.wireOp",EDGE,"E66.2.0");Q2=makeQuery(id+"F32.imprint","IMPRINT",FACE,{"disambiguationData":[TD([[makeQuery(id+"F32.imprint","IMPRINT",EDGE,{"derivedFrom":subQ0}),-1.0]])]});}
            var Q3;
            {var subQ1=sQuery(id+"F32.wireOp",EDGE,"E66.1.0");Q3=makeQuery(id+"F32.imprint","IMPRINT",FACE,{"disambiguationData":[TD([[makeQuery(id+"F32.imprint","IMPRINT",EDGE,{"derivedFrom":subQ1}),-1.0]])]});}
            var Q4;
            {var subQ1=sQuery(id+"F32.wireOp",EDGE,"E64");Q4=makeQuery(id+"F32.imprint","IMPRINT",FACE,{"disambiguationData":[TD([[makeQuery(id+"F32.imprint","IMPRINT",EDGE,{"derivedFrom":subQ1}),1.0]])]});}
            var Q5;
            {var subQ1=sQuery(id+"F32.wireOp",EDGE,"E66.19.0");Q5=makeQuery(id+"F32.imprint","IMPRINT",FACE,{"disambiguationData":[TD([[makeQuery(id+"F32.imprint","IMPRINT",EDGE,{"derivedFrom":subQ1}),-1.0]])]});}
            var Q6;
            {var subQ0=sQuery(id+"F32.wireOp",EDGE,"E66.18.0");Q6=makeQuery(id+"F32.imprint","IMPRINT",FACE,{"disambiguationData":[TD([[makeQuery(id+"F32.imprint","IMPRINT",EDGE,{"derivedFrom":subQ0}),-1.0]])]});}
            var Q7;
            {var subQ0=sQuery(id+"F32.wireOp",EDGE,"E66.17.0");Q7=makeQuery(id+"F32.imprint","IMPRINT",FACE,{"disambiguationData":[TD([[makeQuery(id+"F32.imprint","IMPRINT",EDGE,{"derivedFrom":subQ0}),-1.0]])]});}
            var Q8;
            {var subQ1=sQuery(id+"F32.wireOp",EDGE,"E66.16.0");Q8=makeQuery(id+"F32.imprint","IMPRINT",FACE,{"disambiguationData":[TD([[makeQuery(id+"F32.imprint","IMPRINT",EDGE,{"derivedFrom":subQ1}),-1.0]])]});}
            var Q9;
            {var subQ2=sQuery(id+"F32.wireOp",EDGE,"E66.15.0");Q9=makeQuery(id+"F32.imprint","IMPRINT",FACE,{"disambiguationData":[TD([[makeQuery(id+"F32.imprint","IMPRINT",EDGE,{"derivedFrom":subQ2}),-1.0]])]});}
            var Q10;
            {var subQ1=sQuery(id+"F32.wireOp",EDGE,"E66.14.0");Q10=makeQuery(id+"F32.imprint","IMPRINT",FACE,{"disambiguationData":[TD([[makeQuery(id+"F32.imprint","IMPRINT",EDGE,{"derivedFrom":subQ1}),-1.0]])]});}
            var Q11;
            {var subQ0=sQuery(id+"F32.wireOp",EDGE,"E66.13.0");Q11=makeQuery(id+"F32.imprint","IMPRINT",FACE,{"disambiguationData":[TD([[makeQuery(id+"F32.imprint","IMPRINT",EDGE,{"derivedFrom":subQ0}),-1.0]])]});}
            var Q12;
            {var subQ2=sQuery(id+"F32.wireOp",EDGE,"E66.12.0");Q12=makeQuery(id+"F32.imprint","IMPRINT",FACE,{"disambiguationData":[TD([[makeQuery(id+"F32.imprint","IMPRINT",EDGE,{"derivedFrom":subQ2}),-1.0]])]});}
            var Q13;
            {var subQ2=sQuery(id+"F32.wireOp",EDGE,"E66.11.0");Q13=makeQuery(id+"F32.imprint","IMPRINT",FACE,{"disambiguationData":[TD([[makeQuery(id+"F32.imprint","IMPRINT",EDGE,{"derivedFrom":subQ2}),-1.0]])]});}
            var Q14;
            {var subQ1=sQuery(id+"F32.wireOp",EDGE,"E66.10.0");Q14=makeQuery(id+"F32.imprint","IMPRINT",FACE,{"disambiguationData":[TD([[makeQuery(id+"F32.imprint","IMPRINT",EDGE,{"derivedFrom":subQ1}),-1.0]])]});}
            var Q15;
            {var subQ0=sQuery(id+"F32.wireOp",EDGE,"E66.9.0");Q15=makeQuery(id+"F32.imprint","IMPRINT",FACE,{"disambiguationData":[TD([[makeQuery(id+"F32.imprint","IMPRINT",EDGE,{"derivedFrom":subQ0}),-1.0]])]});}
            var Q16;
            {var subQ2=sQuery(id+"F32.wireOp",EDGE,"E66.8.0");Q16=makeQuery(id+"F32.imprint","IMPRINT",FACE,{"disambiguationData":[TD([[makeQuery(id+"F32.imprint","IMPRINT",EDGE,{"derivedFrom":subQ2}),-1.0]])]});}
            var Q17;
            {var subQ1=sQuery(id+"F32.wireOp",EDGE,"E66.7.0");Q17=makeQuery(id+"F32.imprint","IMPRINT",FACE,{"disambiguationData":[TD([[makeQuery(id+"F32.imprint","IMPRINT",EDGE,{"derivedFrom":subQ1}),-1.0]])]});}
            var Q18;
            {var subQ1=sQuery(id+"F32.wireOp",EDGE,"E66.6.0");Q18=makeQuery(id+"F32.imprint","IMPRINT",FACE,{"disambiguationData":[TD([[makeQuery(id+"F32.imprint","IMPRINT",EDGE,{"derivedFrom":subQ1}),-1.0]])]});}
            var Q19;
            {var subQ1=sQuery(id+"F32.wireOp",EDGE,"E66.5.0");Q19=makeQuery(id+"F32.imprint","IMPRINT",FACE,{"disambiguationData":[TD([[makeQuery(id+"F32.imprint","IMPRINT",EDGE,{"derivedFrom":subQ1}),-1.0]])]});}
            var Q20;
            {var subQ1=sQuery(id+"F32.wireOp",EDGE,"E66.4.0");Q20=makeQuery(id+"F32.imprint","IMPRINT",FACE,{"disambiguationData":[TD([[makeQuery(id+"F32.imprint","IMPRINT",EDGE,{"derivedFrom":subQ1}),-1.0]])]});}
            var Q21;
            {var subQ0=sQuery(id+"F32.wireOp",EDGE,"E66.3.0");Q21=makeQuery(id+"F32.imprint","IMPRINT",FACE,{"disambiguationData":[TD([[makeQuery(id+"F32.imprint","IMPRINT",EDGE,{"derivedFrom":subQ0}),-1.0]])]});}
            extrude(context, id + "F33", {"entities" : qUnion([Q0, Q1, Q2, Q3, Q4, Q5, Q6, Q7, Q8, Q9, Q10, Q11, Q12, Q13, Q14, Q15, Q16, Q17, Q18, Q19, Q20, Q21]), "depth" : 5 * mm});
        }
        {
            var Q0;
            Q0=qCreatedBy(makeId("Front.planeOp"),FACE);
            var sketch = newSketch(context, id + "F34", { "sketchPlane" : qUnion([Q0])});
            skLineSegment(sketch, "E67.0", {"start": v(5, 11.5) * mm, "end": v(5, -11.5) * mm});
            skLineSegment(sketch, "E67.1", {"start": v(5, 12.75) * mm, "end": v(5, -12.75) * mm});
            skLineSegment(sketch, "E67.2", {"start": v(5, 14) * mm, "end": v(5, -14) * mm});
            skLineSegment(sketch, "E68.bottom", {"start": v(5, 11.5) * mm, "end": v(10, 11.5) * mm});
            skLineSegment(sketch, "E68.top", {"start": v(5, 14) * mm, "end": v(10, 14) * mm});
            skLineSegment(sketch, "E68.left", {"start": v(5, 11.5) * mm, "end": v(5, 14) * mm});
            skLineSegment(sketch, "E68.right", {"start": v(10, 11.5) * mm, "end": v(10, 14) * mm});
            skLineSegment(sketch, "E69", {"start": v(7.5, 14) * mm, "end": v(7.5, 11.5) * mm, "construction": true});
            skLineSegment(sketch, "E70", {"start": v(5, 11.5) * mm, "end": v(15, 11.5) * mm, "construction": true});
            skArc(sketch, "E71", {"start": v(5.24, 14) * mm, "mid": v(5.1, 13.38) * mm, "end": v(5, 12.75) * mm});
            skArc(sketch, "E72.0.MirrorCS", {"start": v(9.76, 14) * mm, "mid": v(9.9, 13.38) * mm, "end": v(10, 12.75) * mm});
            skLineSegment(sketch, "E73", {"start": v(5, 0) * mm, "end": v(9.68, 0) * mm});
            skSolve(sketch);
        }
        {
            var Q0;
            {var subQ0=sQuery(id+"F34.wireOp",EDGE,"E71");Q0=makeQuery(id+"F34.imprint","IMPRINT",FACE,{"disambiguationData":[TD([[makeQuery(id+"F34.imprint","IMPRINT",EDGE,{"derivedFrom":subQ0}),-1.0]])]});}
            var Q1;
            {var subQ0=sQuery(id+"F34.wireOp",EDGE,"E72.0.MirrorCS");Q1=makeQuery(id+"F34.imprint","IMPRINT",FACE,{"disambiguationData":[TD([[makeQuery(id+"F34.imprint","IMPRINT",EDGE,{"derivedFrom":subQ0}),1.0]])]});}
            var Q2;
            Q2=sQuery(id+"F34.wireOp",EDGE,"E73");
            revolve(context, id + "F35", {"operationType" : NewBodyOperationType.REMOVE, "entities" : qUnion([Q0, Q1]), "axis" : qUnion([Q2]), "revolveType" : RevolveType.FULL, "oppositeDirection" : true});
        }
    });
